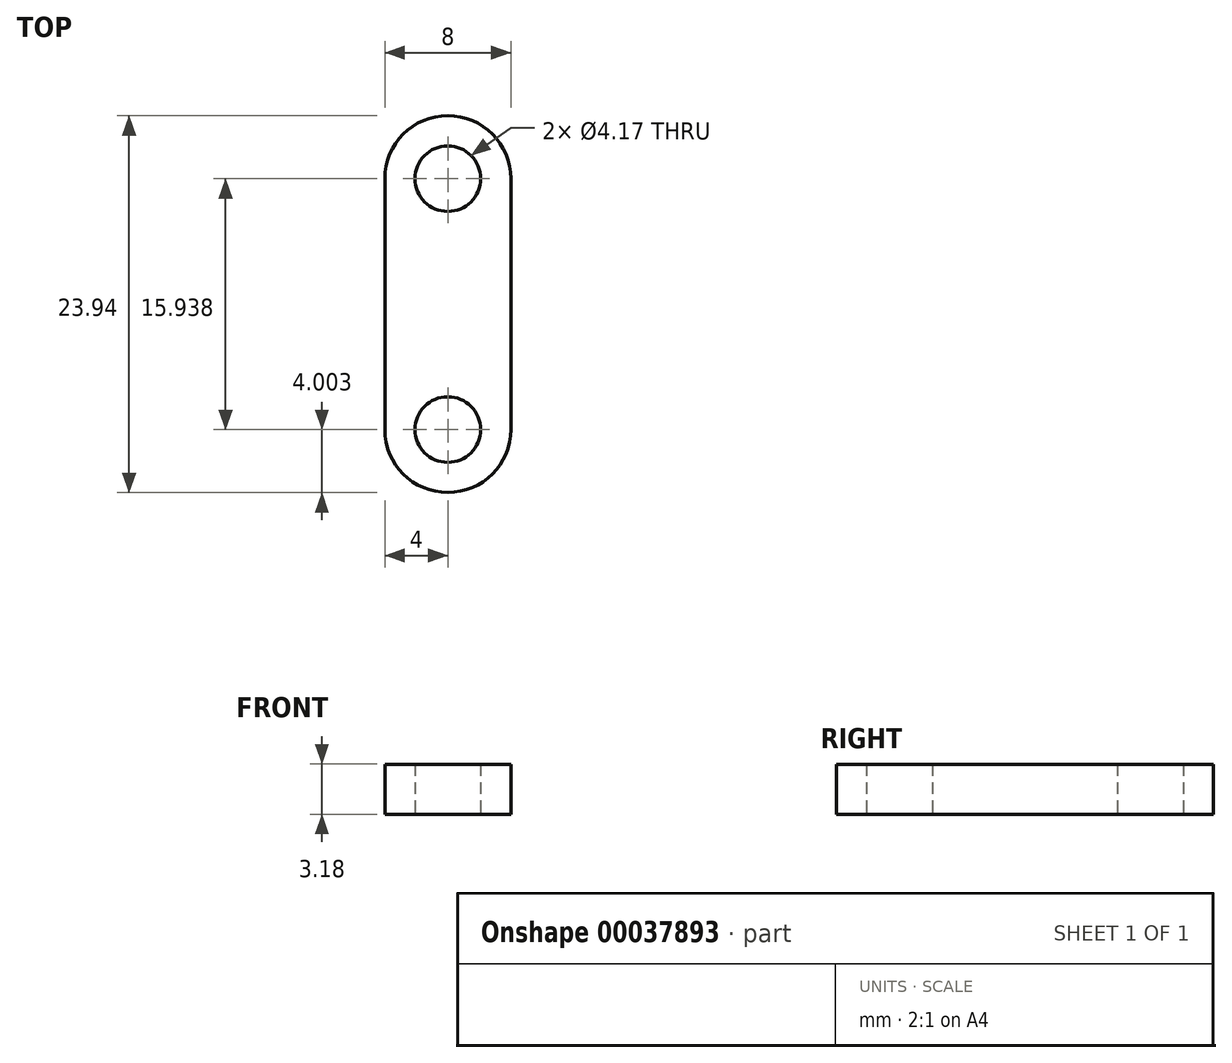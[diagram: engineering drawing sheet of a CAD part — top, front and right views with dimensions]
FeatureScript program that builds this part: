
annotation { "Feature Type Name" : "Feature", "Feature Type Description" : "" }
export const myFeature = defineFeature(function(context is Context, id is Id, definition is map)
    precondition{}
    {
        {
            var Q0;
            Q0=qCreatedBy(makeId("Top.planeOp"),FACE);
            var sketch = newSketch(context, id + "F0", { "sketchPlane" : qUnion([Q0])});
            skLineSegment(sketch, "E0.bottom", {"start": v(0, 0) * mm, "end": v(8, 0) * mm, "construction": true});
            skLineSegment(sketch, "E0.top", {"start": v(0, -15.94) * mm, "end": v(8, -15.94) * mm, "construction": true});
            skLineSegment(sketch, "E0.left", {"start": v(0, 0) * mm, "end": v(0, -15.94) * mm});
            skLineSegment(sketch, "E0.right", {"start": v(8, 0) * mm, "end": v(8, -15.94) * mm});
            skLineSegment(sketch, "E1", {"start": v(4, 0) * mm, "end": v(4, -15.94) * mm, "construction": true});
            skArc(sketch, "E2", {"start": v(8, 0) * mm, "mid": v(4, 4) * mm, "end": v(0, 0) * mm});
            skArc(sketch, "E3", {"start": v(0, -15.94) * mm, "mid": v(4, -19.94) * mm, "end": v(8, -15.94) * mm});
            skCircle(sketch, "E4", {"center": v(4, 0) * mm, "radius": 2.08 * mm});
            skCircle(sketch, "E5", {"center": v(4, -15.94) * mm, "radius": 2.08 * mm});
            skSolve(sketch);
        }
        {
            var Q0;
            Q0 = qSketchRegion(id + "F0", true);
            extrude(context, id + "F1", {"entities" : qUnion([Q0]), "depth" : 3.17 * mm});
        }
    });
